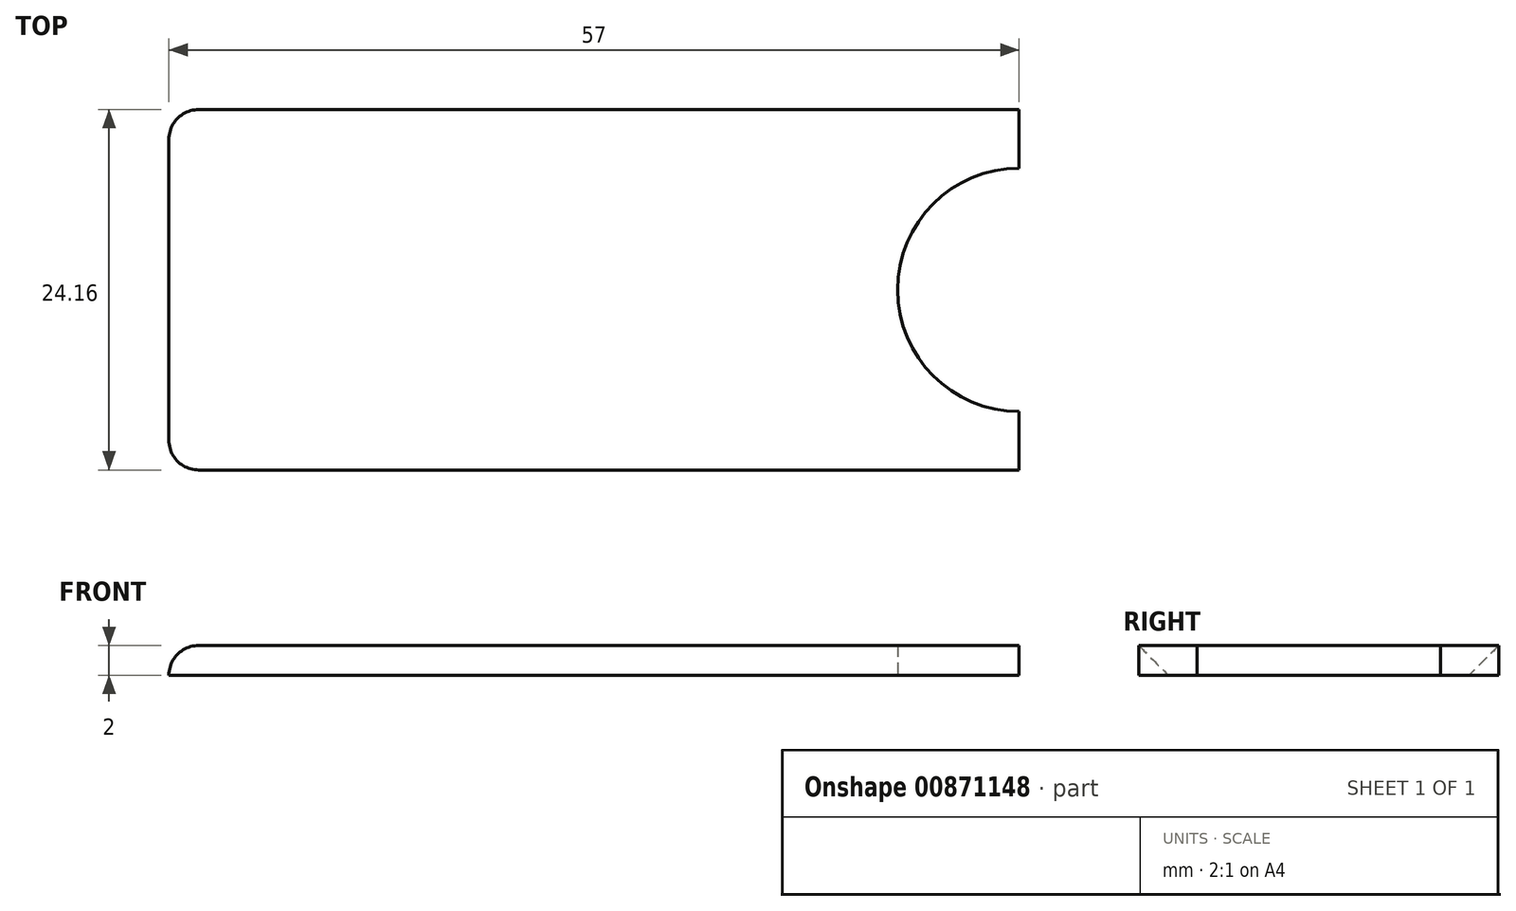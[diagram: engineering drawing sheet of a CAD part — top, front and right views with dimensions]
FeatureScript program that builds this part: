
annotation { "Feature Type Name" : "Feature", "Feature Type Description" : "" }
export const myFeature = defineFeature(function(context is Context, id is Id, definition is map)
    precondition{}
    {
        {
            var Q0;
            Q0=qCreatedBy(makeId("Top.planeOp"),FACE);
            var sketch = newSketch(context, id + "F0", { "sketchPlane" : qUnion([Q0])});
            skLineSegment(sketch, "E0.bottom", {"start": v(22.8, -12.08) * mm, "end": v(-34.2, -12.08) * mm});
            skLineSegment(sketch, "E0.top", {"start": v(22.8, 12.08) * mm, "end": v(-34.2, 12.08) * mm});
            skLineSegment(sketch, "E0.left", {"start": v(22.8, -12.08) * mm, "end": v(22.8, 12.08) * mm});
            skLineSegment(sketch, "E0.right", {"start": v(-34.2, -12.08) * mm, "end": v(-34.2, 12.08) * mm});
            skCircle(sketch, "E1", {"center": v(22.8, 0) * mm, "radius": 8.15 * mm});
            skSolve(sketch);
        }
        {
            var Q0;
            {var subQ4=sQuery(id+"F0.wireOp",EDGE,"E0.bottom");Q0=makeQuery(id+"F0.imprint","IMPRINT",FACE,{"disambiguationData":[TD([[makeQuery(id+"F0.imprint","IMPRINT",EDGE,{"derivedFrom":subQ4}),-1.0]])]});}
            extrude(context, id + "F1", {"entities" : qUnion([Q0]), "depth" : 2 * mm, "offsetDistance" : 25 * mm});
        }
        {
            var Q0;
            Q0=makeQuery(id+"F1.opExtrude","SWEPT_EDGE",EDGE,{"disambiguationData":[OSD([sQuery(id+"F0.wireOp",EDGE,"E0.bottom"),sQuery(id+"F0.wireOp",EDGE,"E0.right")])]});
            var Q1;
            Q1=makeQuery(id+"F1.opExtrude","SWEPT_EDGE",EDGE,{"disambiguationData":[OSD([sQuery(id+"F0.wireOp",EDGE,"E0.top"),sQuery(id+"F0.wireOp",EDGE,"E0.right")])]});
            var Q2;
            Q2=makeQuery(id+"F1.opExtrude","CAP_EDGE",EDGE,{"disambiguationData":[OSD([sQuery(id+"F0.wireOp",EDGE,"E0.right")])],"isStart":false});
            fillet(context, id + "F2", {"entities" : qUnion([Q0, Q1, Q2]), "radius" : 2 * mm, "tangentPropagation" : true, "allowEdgeOverflow" : false});
        }
    });
